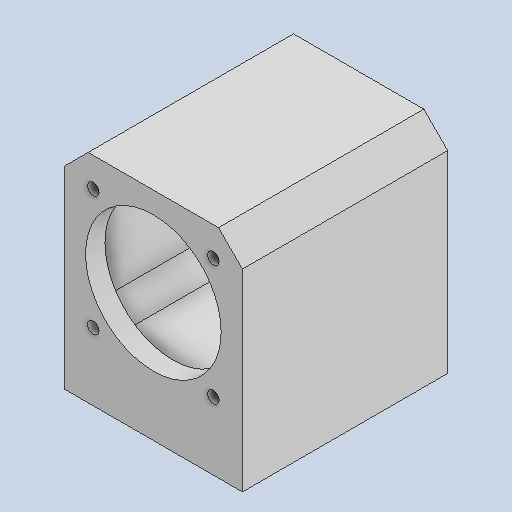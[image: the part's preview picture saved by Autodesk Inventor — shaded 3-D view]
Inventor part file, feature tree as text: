
AUTODESK INVENTOR PART (.ipt)
format: ipt  version: 2024.2 (Build 282272000, 272)  size: 156,160 bytes
history: native  units: in
note: dims shown in document units (in); Inventor stores cm internally (conversion verified against a paired STEP export)
features: sketch x4, other x3
ambient origin geometry x8: Origin, YZ Plane, XZ Plane, XY Plane, X Axis, Y Axis, Z Axis, Center Point
bodies: Solid1 (feature_tree)
feature tree (7):
  other  "support_moteur_v3.ipt"
  other  "Solid1::support_moteur_v3.ipt"
  other  "FonctionRepérage1"
  sketch  "Sketch1"  dims[d0=0.3937in]
  sketch  "Sketch2"
  sketch  "Sketch3"
  sketch  "Sketch4"
